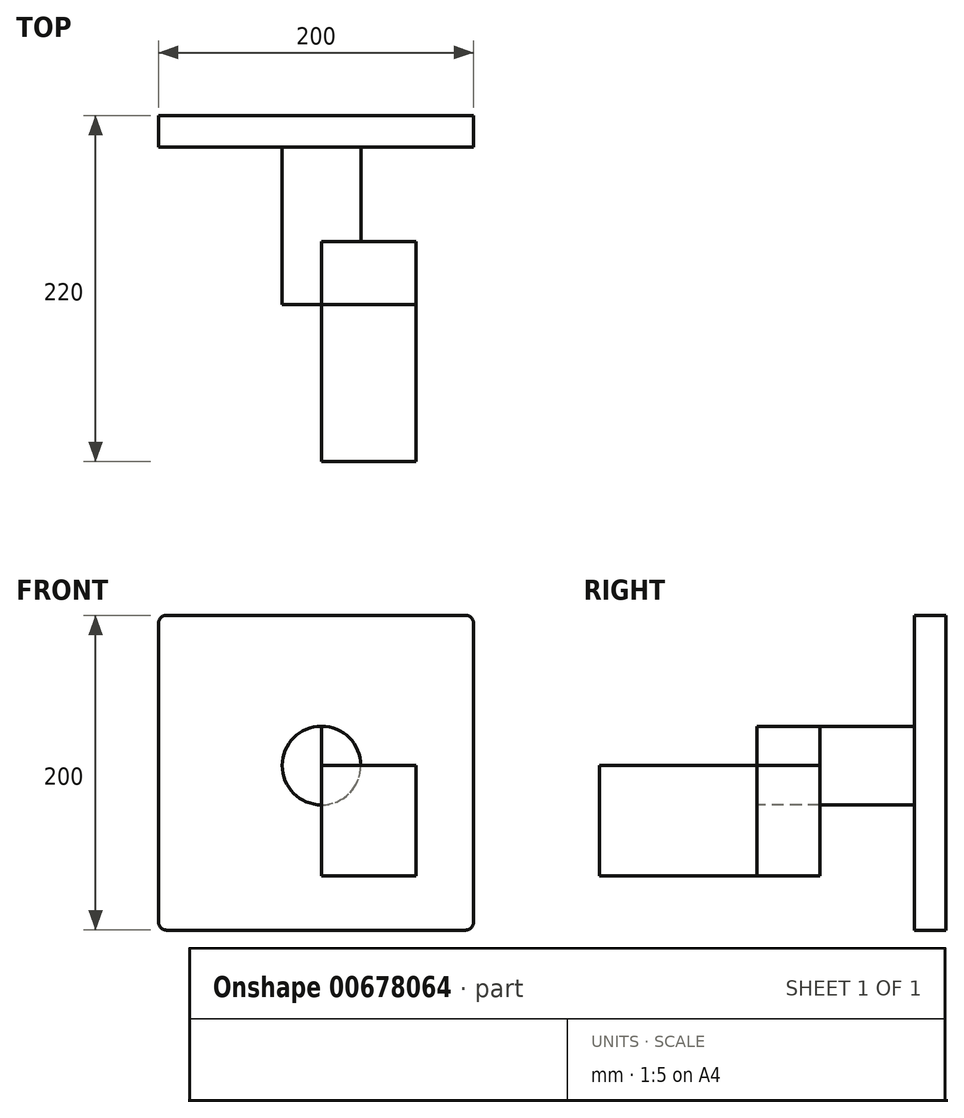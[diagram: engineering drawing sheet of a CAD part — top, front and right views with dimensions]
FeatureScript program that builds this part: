
annotation { "Feature Type Name" : "Feature", "Feature Type Description" : "" }
export const myFeature = defineFeature(function(context is Context, id is Id, definition is map)
    precondition{}
    {
        {
            var Q0;
            Q0=qCreatedBy(makeId("Front.planeOp"),FACE);
            var sketch = newSketch(context, id + "F0", { "sketchPlane" : qUnion([Q0])});
            skLineSegment(sketch, "E0.bottom", {"start": v(-187.5, 171.5) * mm, "end": v(12.5, 171.5) * mm});
            skLineSegment(sketch, "E0.top", {"start": v(-187.5, -28.5) * mm, "end": v(12.5, -28.5) * mm});
            skLineSegment(sketch, "E0.left", {"start": v(-187.5, 171.5) * mm, "end": v(-187.5, -28.5) * mm});
            skLineSegment(sketch, "E0.right", {"start": v(12.5, 171.5) * mm, "end": v(12.5, -28.5) * mm});
            skSolve(sketch);
        }
        {
            var Q0;
            Q0 = qSketchRegion(id + "F0", true);
            extrude(context, id + "F1", {"entities" : qUnion([Q0]), "depth" : 20 * mm, "offsetDistance" : 25 * mm});
        }
        {
            var Q0;
            Q0=makeQuery(id+"F1.opExtrude","SWEPT_EDGE",EDGE,{"disambiguationData":[OSD([sQuery(id+"F0.wireOp",EDGE,"E0.bottom"),sQuery(id+"F0.wireOp",EDGE,"E0.right")])]});
            var Q1;
            Q1=makeQuery(id+"F1.opExtrude","SWEPT_EDGE",EDGE,{"disambiguationData":[OSD([sQuery(id+"F0.wireOp",EDGE,"E0.bottom"),sQuery(id+"F0.wireOp",EDGE,"E0.left")])]});
            var Q2;
            Q2=makeQuery(id+"F1.opExtrude","SWEPT_EDGE",EDGE,{"disambiguationData":[OSD([sQuery(id+"F0.wireOp",EDGE,"E0.top"),sQuery(id+"F0.wireOp",EDGE,"E0.left")])]});
            var Q3;
            Q3=makeQuery(id+"F1.opExtrude","SWEPT_EDGE",EDGE,{"disambiguationData":[OSD([sQuery(id+"F0.wireOp",EDGE,"E0.top"),sQuery(id+"F0.wireOp",EDGE,"E0.right")])]});
            fillet(context, id + "F2", {"entities" : qUnion([Q0, Q1, Q2, Q3]), "radius" : 5 * mm, "tangentPropagation" : true, "allowEdgeOverflow" : false});
        }
        {
            var Q0;
            Q0=makeQuery(id+"F1.opExtrude","CAP_FACE",FACE,{"disambiguationData":[OSD([sQuery(id+"F0.wireOp",EDGE,"E0.bottom"),sQuery(id+"F0.wireOp",EDGE,"E0.top"),sQuery(id+"F0.wireOp",EDGE,"E0.left"),sQuery(id+"F0.wireOp",EDGE,"E0.right")])],"isStart":false});
            var sketch = newSketch(context, id + "F3", { "sketchPlane" : qUnion([Q0])});
            skCircle(sketch, "E1", {"center": v(-84.01, 76.03) * mm, "radius": 25 * mm});
            skSolve(sketch);
        }
        {
            var Q0;
            Q0=makeQuery(id+"F3.imprint","IMPRINT",FACE,{"disambiguationData":[TD([[makeQuery(id+"F3.imprint","IMPRINT",EDGE,{"derivedFrom":sQuery(id+"F3.wireOp",EDGE,"E1")}),1.0]])]});
            extrude(context, id + "F4", {"entities" : qUnion([Q0]), "operationType" : NewBodyOperationType.ADD, "depth" : 100 * mm, "offsetDistance" : 25 * mm});
        }
        {
            var Q0;
            Q0=makeQuery(id+"F4.opExtrude","CAP_FACE",FACE,{"disambiguationData":[OSD([sQuery(id+"F3.wireOp",EDGE,"E1")])],"isStart":false});
            var sketch = newSketch(context, id + "F5", { "sketchPlane" : qUnion([Q0])});
            skLineSegment(sketch, "E2.bottom", {"start": v(-84.01, 76.03) * mm, "end": v(-58.1, 76.03) * mm});
            skLineSegment(sketch, "E2.top", {"start": v(-84.01, 20.31) * mm, "end": v(-58.1, 20.31) * mm});
            skLineSegment(sketch, "E2.left", {"start": v(-84.01, 76.03) * mm, "end": v(-84.01, 20.31) * mm});
            skLineSegment(sketch, "E2.right", {"start": v(-58.1, 76.03) * mm, "end": v(-58.1, 20.31) * mm});
            skLineSegment(sketch, "E3.bottom", {"start": v(-84.01, 76.03) * mm, "end": v(-57.56, 76.03) * mm});
            skLineSegment(sketch, "E3.top", {"start": v(-84.01, 110.6) * mm, "end": v(-57.56, 110.6) * mm});
            skLineSegment(sketch, "E3.left", {"start": v(-84.01, 76.03) * mm, "end": v(-84.01, 110.6) * mm});
            skLineSegment(sketch, "E3.right", {"start": v(-57.56, 76.03) * mm, "end": v(-57.56, 110.6) * mm});
            skSolve(sketch);
        }
        {
            var Q0;
            {var subQ1=sQuery(id+"F5.wireOp",EDGE,"E2.left");var subQ3=makeQuery(id+"F4.opExtrude","CAP_EDGE",EDGE,{"disambiguationData":[OSD([sQuery(id+"F3.wireOp",EDGE,"E1")])],"isStart":false});var subQ4=makeQuery(id+"F5.imprint","INTERSECT",VERTEX,{"derivedFrom":[subQ3,subQ1]});Q0=makeQuery(id+"F5.imprint","IMPRINT",FACE,{"disambiguationData":[TD([[makeQuery(id+"F5.imprint","IMPRINT",EDGE,{"disambiguationData":[TD([[subQ4,-1.0]])],"derivedFrom":subQ3}),1.0]])]});}
            var Q1;
            {var subQ0=sQuery(id+"F5.wireOp",EDGE,"E3.left");var subQ3=makeQuery(id+"F4.opExtrude","CAP_EDGE",EDGE,{"disambiguationData":[OSD([sQuery(id+"F3.wireOp",EDGE,"E1")])],"isStart":false});var subQ5=makeQuery(id+"F5.imprint","INTERSECT",VERTEX,{"derivedFrom":[subQ3,subQ0]});Q1=makeQuery(id+"F5.imprint","IMPRINT",FACE,{"disambiguationData":[TD([[makeQuery(id+"F5.imprint","IMPRINT",EDGE,{"disambiguationData":[TD([[subQ5,1.0]])],"derivedFrom":subQ3}),1.0]])]});}
            extrude(context, id + "F6", {"entities" : qUnion([Q0, Q1]), "operationType" : NewBodyOperationType.REMOVE, "oppositeDirection" : true, "depth" : 40 * mm, "offsetDistance" : 25 * mm});
        }
        {
            var Q0;
            Q0=makeQuery(id+"F4.opExtrude","CAP_FACE",FACE,{"disambiguationData":[OSD([sQuery(id+"F3.wireOp",EDGE,"E1")])],"isStart":false});
            var sketch = newSketch(context, id + "F7", { "sketchPlane" : qUnion([Q0])});
            skLineSegment(sketch, "E4.bottom", {"start": v(-84.01, 76.03) * mm, "end": v(-24.01, 76.03) * mm});
            skLineSegment(sketch, "E4.top", {"start": v(-84.01, 6.03) * mm, "end": v(-24.01, 6.03) * mm});
            skLineSegment(sketch, "E4.left", {"start": v(-84.01, 76.03) * mm, "end": v(-84.01, 6.03) * mm});
            skLineSegment(sketch, "E4.right", {"start": v(-24.01, 76.03) * mm, "end": v(-24.01, 6.03) * mm});
            skLineSegment(sketch, "E5.top", {"start": v(-84.01, 146.03) * mm, "end": v(-24.01, 146.03) * mm});
            skLineSegment(sketch, "E5.left", {"start": v(-84.01, 76.03) * mm, "end": v(-84.01, 146.03) * mm});
            skLineSegment(sketch, "E5.right", {"start": v(-24.01, 76.03) * mm, "end": v(-24.01, 146.03) * mm});
            skSolve(sketch);
        }
        {
            var Q0;
            {var subQ2=sQuery(id+"F7.wireOp",EDGE,"E4.top");Q0=makeQuery(id+"F7.imprint","IMPRINT",FACE,{"disambiguationData":[TD([[makeQuery(id+"F7.imprint","IMPRINT",EDGE,{"derivedFrom":subQ2}),1.0]])]});}
            extrude(context, id + "F8", {"entities" : qUnion([Q0]), "depth" : 50 * mm, "offsetDistance" : 25 * mm});
        }
        {
            var Q0;
            {var subQ2=sQuery(id+"F7.wireOp",EDGE,"E4.top");Q0=makeQuery(id+"F7.imprint","IMPRINT",FACE,{"disambiguationData":[TD([[makeQuery(id+"F7.imprint","IMPRINT",EDGE,{"derivedFrom":subQ2}),1.0]])]});}
            var Q1;
            {var subQ3=sQuery(id+"F7.wireOp",EDGE,"E4.bottom");Q1=makeQuery(id+"F7.imprint","IMPRINT",FACE,{"disambiguationData":[TD([[makeQuery(id+"F7.imprint","IMPRINT",EDGE,{"derivedFrom":subQ3}),1.0]])]});}
            extrude(context, id + "F9", {"entities" : qUnion([Q0, Q1]), "operationType" : NewBodyOperationType.ADD, "depth" : 50 * mm, "offsetDistance" : 25 * mm});
        }
        {
            var Q0;
            {var subQ0=sQuery(id+"F7.wireOp",EDGE,"E4.right");var subQ1=sQuery(id+"F7.wireOp",EDGE,"E4.left");var subQ2=sQuery(id+"F7.wireOp",EDGE,"E4.top");Q0=makeQuery(id+"F9.boolean.opBoolean","MERGE",FACE,{"derivedFrom":[makeQuery(id+"F8.opExtrude","CAP_FACE",FACE,{"disambiguationData":[OSD([subQ2,subQ1,subQ0,sQuery(id+"F7.wireOp",EDGE,"E4.bottom")])],"isStart":true}),makeQuery(id+"F9.opExtrude","CAP_FACE",FACE,{"disambiguationData":[OSD([subQ2,subQ1,subQ0,sQuery(id+"F7.wireOp",EDGE,"E5.top"),sQuery(id+"F7.wireOp",EDGE,"E5.left"),sQuery(id+"F7.wireOp",EDGE,"E5.right")])],"isStart":true})]});}
            extrude(context, id + "F10", {"entities" : qUnion([Q0]), "depth" : 40 * mm, "offsetDistance" : 25 * mm});
        }
        {
            var Q0;
            {var subQ0=sQuery(id+"F7.wireOp",EDGE,"E4.right");var subQ1=sQuery(id+"F7.wireOp",EDGE,"E4.left");var subQ2=sQuery(id+"F7.wireOp",EDGE,"E4.top");Q0=makeQuery(id+"F9.boolean.opBoolean","MERGE",FACE,{"derivedFrom":[makeQuery(id+"F8.opExtrude","CAP_FACE",FACE,{"disambiguationData":[OSD([subQ2,subQ1,subQ0,sQuery(id+"F7.wireOp",EDGE,"E4.bottom")])],"isStart":false}),makeQuery(id+"F9.opExtrude","CAP_FACE",FACE,{"disambiguationData":[OSD([subQ2,subQ1,subQ0,sQuery(id+"F7.wireOp",EDGE,"E5.top"),sQuery(id+"F7.wireOp",EDGE,"E5.left"),sQuery(id+"F7.wireOp",EDGE,"E5.right")])],"isStart":false})]});}
            extrude(context, id + "F11", {"entities" : qUnion([Q0]), "operationType" : NewBodyOperationType.ADD, "depth" : 50 * mm, "offsetDistance" : 25 * mm});
        }
    });
